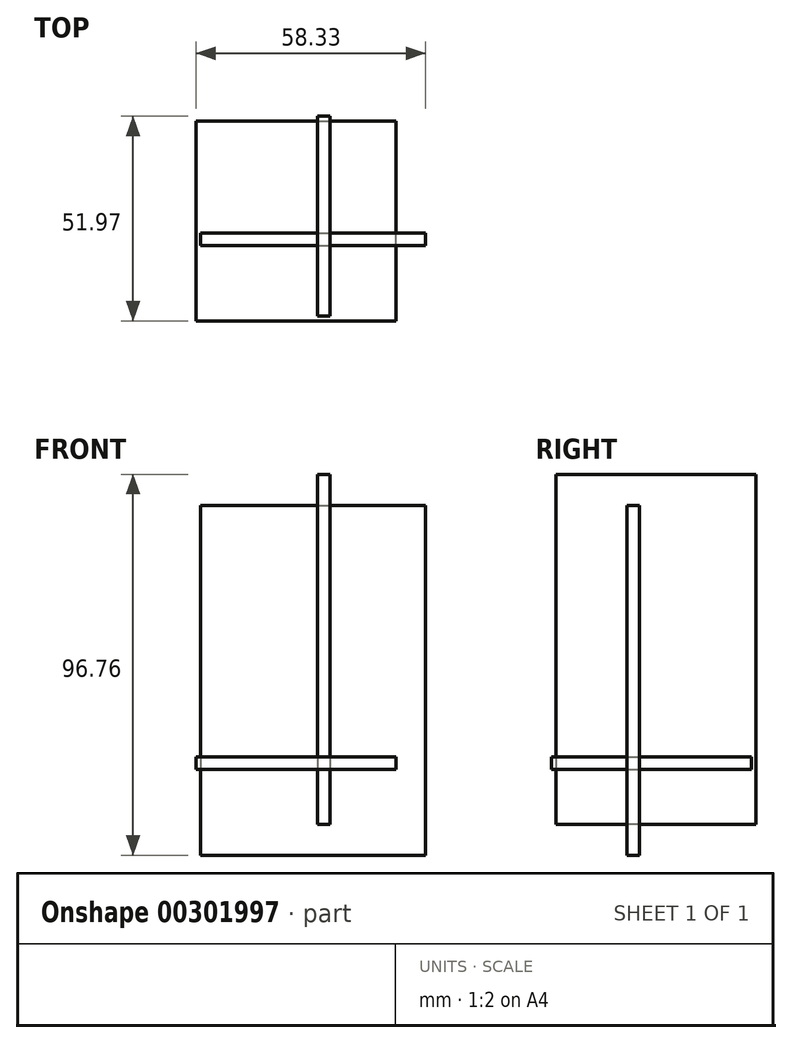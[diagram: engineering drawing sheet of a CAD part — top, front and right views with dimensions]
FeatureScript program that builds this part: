
annotation { "Feature Type Name" : "Feature", "Feature Type Description" : "" }
export const myFeature = defineFeature(function(context is Context, id is Id, definition is map)
    precondition{}
    {
        {
            var Q0;
            Q0=qCreatedBy(makeId("Front.planeOp"),FACE);
            var sketch = newSketch(context, id + "F0", { "sketchPlane" : qUnion([Q0])});
            skLineSegment(sketch, "E0.bottom", {"start": v(-29.63, 67.16) * mm, "end": v(27.52, 67.16) * mm});
            skLineSegment(sketch, "E0.top", {"start": v(-29.63, -21.74) * mm, "end": v(27.52, -21.74) * mm});
            skLineSegment(sketch, "E0.left", {"start": v(-29.63, 67.16) * mm, "end": v(-29.63, -21.74) * mm});
            skLineSegment(sketch, "E0.right", {"start": v(27.52, 67.16) * mm, "end": v(27.52, -21.74) * mm});
            skSolve(sketch);
        }
        {
            var Q0;
            Q0=qSketchRegion(id+"F0",true);
            extrude(context, id + "F1", {"entities" : qUnion([Q0]), "depth" : 3.17 * mm});
        }
        {
            var Q0;
            Q0=qCreatedBy(makeId("Right.planeOp"),FACE);
            var sketch = newSketch(context, id + "F2", { "sketchPlane" : qUnion([Q0])});
            skLineSegment(sketch, "E1.bottom", {"start": v(29.61, 75.02) * mm, "end": v(-21.19, 75.02) * mm});
            skLineSegment(sketch, "E1.top", {"start": v(29.61, -13.88) * mm, "end": v(-21.19, -13.88) * mm});
            skLineSegment(sketch, "E1.left", {"start": v(29.61, 75.02) * mm, "end": v(29.61, -13.88) * mm});
            skLineSegment(sketch, "E1.right", {"start": v(-21.19, 75.02) * mm, "end": v(-21.19, -13.88) * mm});
            skSolve(sketch);
        }
        {
            var Q0;
            Q0=qSketchRegion(id+"F2",true);
            extrude(context, id + "F3", {"entities" : qUnion([Q0]), "depth" : 3.17 * mm});
        }
        {
            var Q0;
            Q0=qCreatedBy(makeId("Top.planeOp"),FACE);
            var sketch = newSketch(context, id + "F4", { "sketchPlane" : qUnion([Q0])});
            skLineSegment(sketch, "E2.bottom", {"start": v(-30.81, -22.36) * mm, "end": v(19.99, -22.36) * mm});
            skLineSegment(sketch, "E2.top", {"start": v(-30.81, 28.44) * mm, "end": v(19.99, 28.44) * mm});
            skLineSegment(sketch, "E2.left", {"start": v(-30.81, -22.36) * mm, "end": v(-30.81, 28.44) * mm});
            skLineSegment(sketch, "E2.right", {"start": v(19.99, -22.36) * mm, "end": v(19.99, 28.44) * mm});
            skSolve(sketch);
        }
        {
            var Q0;
            Q0=qSketchRegion(id+"F4",true);
            extrude(context, id + "F5", {"entities" : qUnion([Q0]), "depth" : 3.17 * mm});
        }
    });
